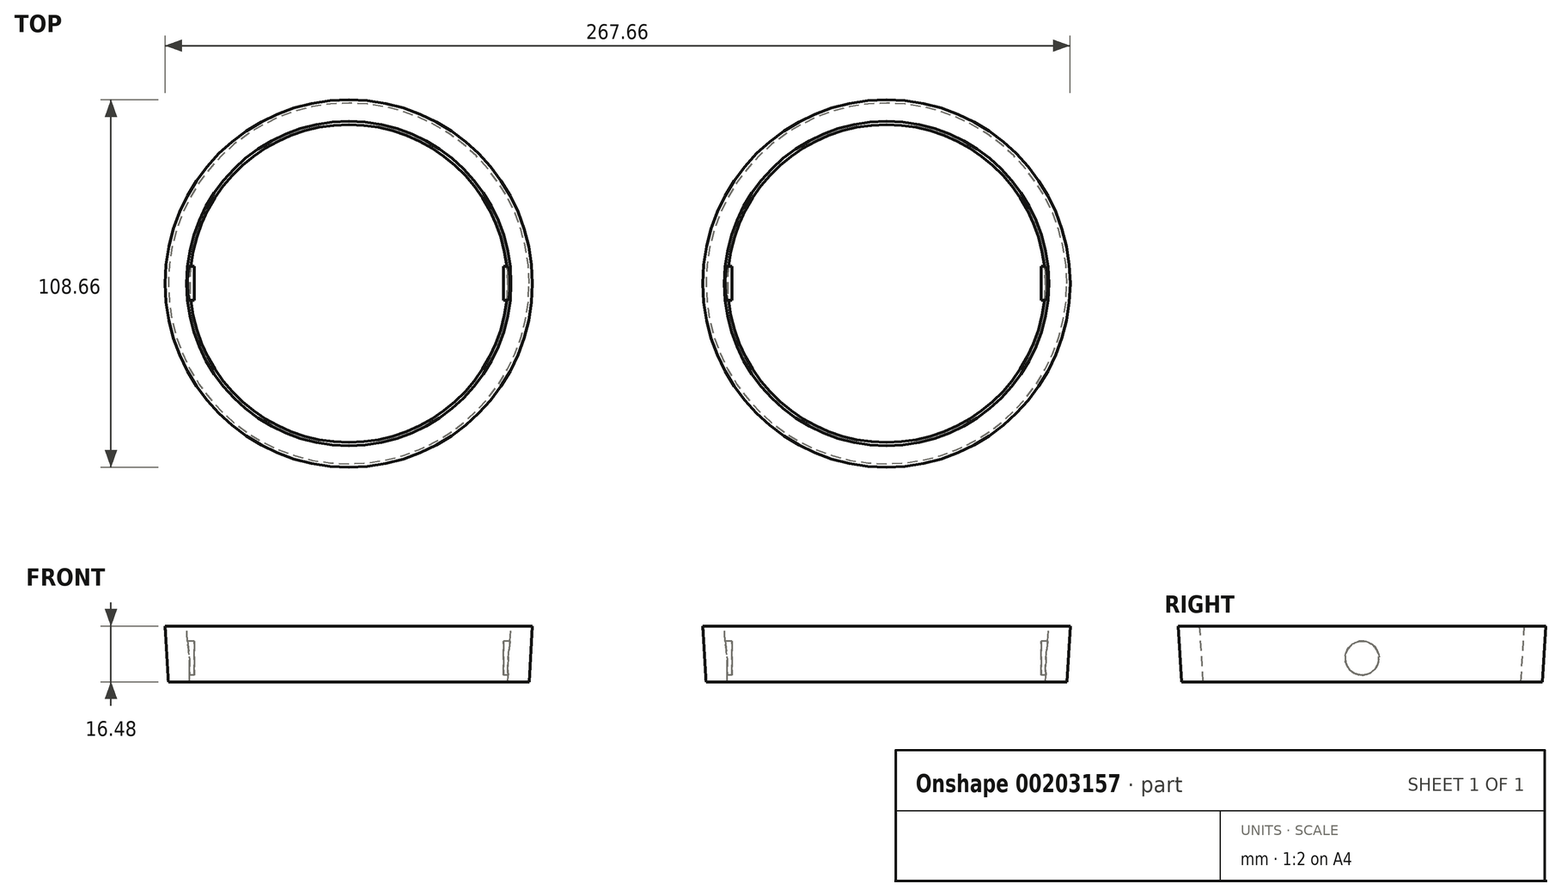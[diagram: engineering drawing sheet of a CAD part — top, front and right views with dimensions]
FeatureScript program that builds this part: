
annotation { "Feature Type Name" : "Feature", "Feature Type Description" : "" }
export const myFeature = defineFeature(function(context is Context, id is Id, definition is map)
    precondition{}
    {
        {
            var Q0;
            Q0=qCreatedBy(makeId("Front.planeOp"),FACE);
            var sketch = newSketch(context, id + "F0", { "sketchPlane" : qUnion([Q0])});
            skLineSegment(sketch, "E0", {"start": v(-47, -16.48) * mm, "end": v(-53.35, -16.48) * mm});
            skLineSegment(sketch, "E1", {"start": v(-53.35, -16.48) * mm, "end": v(-54.33, 0) * mm});
            skLineSegment(sketch, "E2", {"start": v(-54.33, 0) * mm, "end": v(-47.98, 0) * mm});
            skLineSegment(sketch, "E3", {"start": v(-47.98, 0) * mm, "end": v(-47, -16.48) * mm});
            skLineSegment(sketch, "E4", {"start": v(-47, -16.48) * mm, "end": v(-47, 9.83) * mm});
            skLineSegment(sketch, "E5", {"start": v(-47, 9.83) * mm, "end": v(-47, -16.48) * mm});
            skLineSegment(sketch, "E6", {"start": v(0, 16.35) * mm, "end": v(0, -18.43) * mm});
            skLineSegment(sketch, "E7", {"start": v(0, -18.43) * mm, "end": v(0, 16.35) * mm});
            skSolve(sketch);
        }
        {
            var Q0;
            Q0=makeQuery(id+"F0.imprint","IMPRINT",FACE,{"disambiguationData":[TD([[makeQuery(id+"F0.imprint","IMPRINT",EDGE,{"derivedFrom":sQuery(id+"F0.wireOp",EDGE,"E0")}),-1.0]])]});
            var Q1;
            Q1=sQuery(id+"F0.wireOp",EDGE,"E7");
            revolve(context, id + "F1", {"entities" : qUnion([Q0]), "axis" : qUnion([Q1]), "revolveType" : RevolveType.FULL});
        }
        {
            var Q0;
            Q0=qCreatedBy(makeId("Right.planeOp"),FACE);
            var sketch = newSketch(context, id + "F2", { "sketchPlane" : qUnion([Q0])});
            skCircle(sketch, "E8", {"center": v(0, -9.46) * mm, "radius": 5.02 * mm});
            skSolve(sketch);
        }
        {
            var Q0;
            Q0=makeQuery(id+"F2.imprint","IMPRINT",FACE,{"disambiguationData":[TD([[makeQuery(id+"F2.imprint","IMPRINT",EDGE,{"derivedFrom":sQuery(id+"F2.wireOp",EDGE,"E8")}),1.0]])]});
            extrude(context, id + "F3", {"entities" : qUnion([Q0]), "operationType" : NewBodyOperationType.ADD, "endBound" : BoundingType.SYMMETRIC, "depth" : 98.9 * mm});
        }
        {
            var Q0;
            Q0=makeQuery(id+"F2.imprint","IMPRINT",FACE,{"disambiguationData":[TD([[makeQuery(id+"F2.imprint","IMPRINT",EDGE,{"derivedFrom":sQuery(id+"F2.wireOp",EDGE,"E8")}),1.0]])]});
            extrude(context, id + "F4", {"entities" : qUnion([Q0]), "operationType" : NewBodyOperationType.REMOVE, "endBound" : BoundingType.SYMMETRIC, "oppositeDirection" : true, "depth" : 91.44 * mm});
        }
        {
            var Q0;
            Q0=makeQuery(id+"F1.opRevolve","SWEPT_BODY",BODY,{"disambiguationData":[OSD([sQuery(id+"F0.wireOp",EDGE,"E0"),sQuery(id+"F0.wireOp",EDGE,"E1"),sQuery(id+"F0.wireOp",EDGE,"E2"),sQuery(id+"F0.wireOp",EDGE,"E3")])]});
            transform(context, id + "F5", {"entities" : qUnion([Q0]), "transformType" : TransformType.TRANSLATION_3D, "dx" : 159 * mm, "dy" : 0 * mm, "dz" : 0 * mm, "makeCopy" : true});
        }
    });
